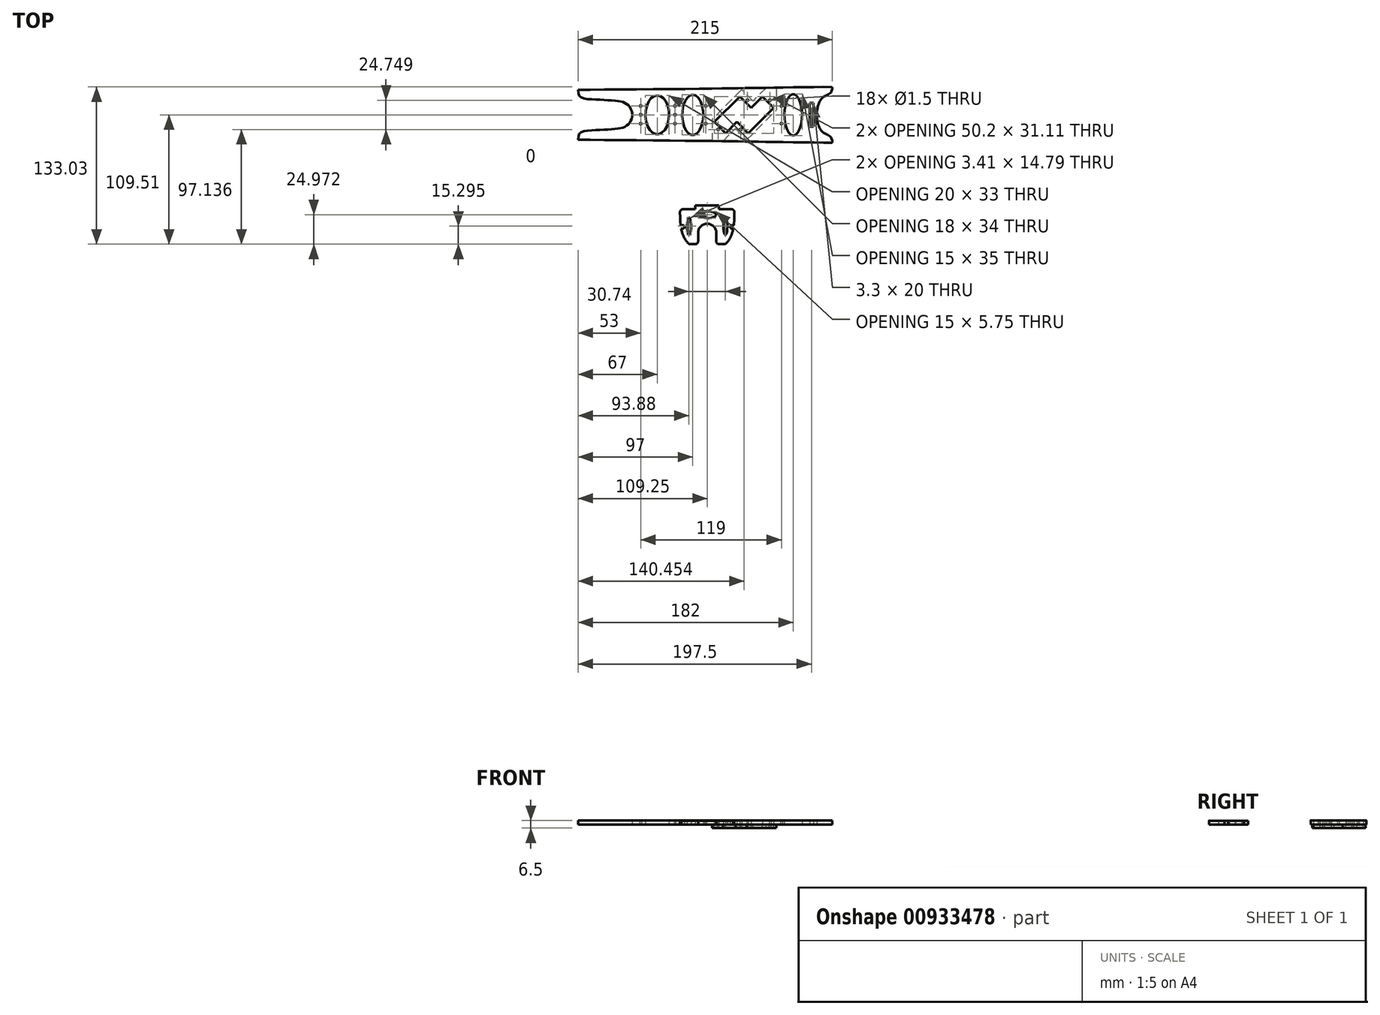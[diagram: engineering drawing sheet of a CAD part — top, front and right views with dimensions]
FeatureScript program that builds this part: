
annotation { "Feature Type Name" : "Feature", "Feature Type Description" : "" }
export const myFeature = defineFeature(function(context is Context, id is Id, definition is map)
    precondition{}
    {
        {
            var Q0;
            Q0=qCreatedBy(makeId("Top.planeOp"),FACE);
            var sketch = newSketch(context, id + "F0", { "sketchPlane" : qUnion([Q0])});
            skLineSegment(sketch, "E0", {"start": v(-109.25, -3.3) * mm, "end": v(-109.25, -45.3) * mm, "construction": true});
            skPoint(sketch, "E1", {"position": v(-109.25, -24.3) * mm});
            skLineSegment(sketch, "E2", {"start": v(105.75, -1.8) * mm, "end": v(105.75, -46.8) * mm, "construction": true});
            skPoint(sketch, "E3", {"position": v(105.75, -24.3) * mm});
            skLineSegment(sketch, "E4", {"start": v(-109.25, -24.3) * mm, "end": v(105.75, -24.3) * mm, "construction": true});
            skPoint(sketch, "E5", {"position": v(0, 0) * mm});
            skSolve(sketch);
        }
        {
            var Q0;
            Q0=qCreatedBy(makeId("Top.planeOp"),FACE);
            var sketch = newSketch(context, id + "F1", { "sketchPlane" : qUnion([Q0])});
            skLineSegment(sketch, "E6.0", {"start": v(-109.25, -3.3) * mm, "end": v(-109.25, -45.3) * mm, "construction": true});
            skLineSegment(sketch, "E7.0", {"start": v(-109.25, -24.3) * mm, "end": v(105.75, -24.3) * mm, "construction": true});
            skLineSegment(sketch, "E8.0", {"start": v(105.75, -0.8) * mm, "end": v(105.75, -46.8) * mm, "construction": true});
            skPoint(sketch, "E9.0", {"position": v(105.75, -24.3) * mm});
            skPoint(sketch, "E10.0", {"position": v(105.75, -1.8) * mm});
            skPoint(sketch, "E11.0", {"position": v(105.75, -46.8) * mm});
            skPoint(sketch, "E12.0", {"position": v(-109.25, -45.3) * mm});
            skPoint(sketch, "E13.0", {"position": v(-109.25, -24.3) * mm});
            skPoint(sketch, "E14.0", {"position": v(-109.25, -3.3) * mm});
            skFitSpline(sketch, "E15", {"points": [v(-109.25, -3.3) * mm, v(-1.69, -2.2) * mm, v(33.76, -1.65) * mm, v(60.11, -1.3) * mm, v(105.75, -0.8) * mm], "startDerivative": vector(214.94, 3.55) * mm, "endDerivative": vector(149.57, -1.3) * mm});
            skFitSpline(sketch, "E16", {"points": [v(-109.25, -3.3) * mm, v(-107.75, -8.59) * mm, v(-103.34, -10.65) * mm, v(-92.47, -11.5) * mm, v(-82.9, -12) * mm, v(-75.3, -12.62) * mm, v(-71.83, -13.28) * mm, v(-68.83, -14.68) * mm, v(-66.4, -16.56) * mm, v(-64.61, -19.28) * mm, v(-63.68, -22.18) * mm, v(-63.5, -24.3) * mm], "startDerivative": vector(0, -79.4) * mm, "endDerivative": vector(0, -33.77) * mm});
            skFitSpline(sketch, "E17", {"points": [v(105.75, -0.8) * mm, v(104.77, -5.14) * mm, v(102.97, -6.7) * mm, v(99.97, -8.21) * mm, v(97.34, -10) * mm, v(95.85, -11.78) * mm, v(94.53, -14.5) * mm, v(93.6, -17.21) * mm, v(93.03, -20.22) * mm, v(92.86, -22.42) * mm, v(92.86, -24.3) * mm], "startDerivative": vector(0, -44.94) * mm, "endDerivative": vector(0, -23.1) * mm});
            skLineSegment(sketch, "E18", {"start": v(37.21, -18.29) * mm, "end": v(27.67, -8.74) * mm});
            skLineSegment(sketch, "E19", {"start": v(27.67, -8.74) * mm, "end": v(6.1, -30.31) * mm});
            skLineSegment(sketch, "E20", {"start": v(6.1, -30.31) * mm, "end": v(15.65, -39.86) * mm});
            skLineSegment(sketch, "E21", {"start": v(15.65, -39.86) * mm, "end": v(37.21, -18.29) * mm});
            skPoint(sketch, "E22", {"position": v(32.44, -13.52) * mm});
            skPoint(sketch, "E23", {"position": v(10.87, -35.08) * mm});
            skLineSegment(sketch, "E24", {"start": v(32.44, -13.52) * mm, "end": v(10.87, -35.08) * mm, "construction": true});
            skCircle(sketch, "E25", {"center": v(26.43, -19.53) * mm, "radius": 17 * mm, "construction": true});
            skPoint(sketch, "E26", {"position": v(21.66, -24.3) * mm});
            skCircle(sketch, "E27", {"center": v(26.43, -19.53) * mm, "radius": 13 * mm, "construction": true});
            skLineSegment(sketch, "E28", {"start": v(6.1, -30.31) * mm, "end": v(2.92, -33.5) * mm, "construction": true});
            skLineSegment(sketch, "E29", {"start": v(2.92, -33.5) * mm, "end": v(12.47, -43.04) * mm, "construction": true});
            skLineSegment(sketch, "E30", {"start": v(12.47, -43.04) * mm, "end": v(15.65, -39.86) * mm, "construction": true});
            skLineSegment(sketch, "E31", {"start": v(27.67, -8.74) * mm, "end": v(30.85, -5.56) * mm, "construction": true});
            skLineSegment(sketch, "E32", {"start": v(30.85, -5.56) * mm, "end": v(40.4, -15.1) * mm, "construction": true});
            skLineSegment(sketch, "E33", {"start": v(40.4, -15.1) * mm, "end": v(37.21, -18.29) * mm, "construction": true});
            skLineSegment(sketch, "E34", {"start": v(25.2, -30.31) * mm, "end": v(34.74, -39.86) * mm});
            skLineSegment(sketch, "E35", {"start": v(34.74, -39.86) * mm, "end": v(56.3, -18.29) * mm});
            skLineSegment(sketch, "E36", {"start": v(56.3, -18.29) * mm, "end": v(46.76, -8.74) * mm});
            skLineSegment(sketch, "E37", {"start": v(46.76, -8.74) * mm, "end": v(25.2, -30.31) * mm});
            skPoint(sketch, "E38", {"position": v(29.97, -35.08) * mm});
            skPoint(sketch, "E39", {"position": v(51.53, -13.52) * mm});
            skLineSegment(sketch, "E40", {"start": v(29.97, -35.08) * mm, "end": v(51.53, -13.52) * mm, "construction": true});
            skCircle(sketch, "E41", {"center": v(35.98, -29.07) * mm, "radius": 17 * mm, "construction": true});
            skPoint(sketch, "E42", {"position": v(40.75, -24.3) * mm});
            skCircle(sketch, "E43", {"center": v(35.98, -29.07) * mm, "radius": 13 * mm, "construction": true});
            skLineSegment(sketch, "E44", {"start": v(56.3, -18.29) * mm, "end": v(59.49, -15.1) * mm, "construction": true});
            skLineSegment(sketch, "E45", {"start": v(59.49, -15.1) * mm, "end": v(49.94, -5.56) * mm, "construction": true});
            skLineSegment(sketch, "E46", {"start": v(49.94, -5.56) * mm, "end": v(46.76, -8.74) * mm, "construction": true});
            skLineSegment(sketch, "E47", {"start": v(34.74, -39.86) * mm, "end": v(31.56, -43.04) * mm, "construction": true});
            skLineSegment(sketch, "E48", {"start": v(31.56, -43.04) * mm, "end": v(22.01, -33.5) * mm, "construction": true});
            skLineSegment(sketch, "E49", {"start": v(22.01, -33.5) * mm, "end": v(25.2, -30.31) * mm, "construction": true});
            skFitSpline(sketch, "E50.MirrorCS", {"points": [v(-109.25, -45.3) * mm, v(-1.69, -46.4) * mm, v(33.76, -46.95) * mm, v(60.11, -47.3) * mm, v(105.75, -47.8) * mm], "startDerivative": vector(214.94, -3.55) * mm, "endDerivative": vector(149.57, 1.3) * mm});
            skFitSpline(sketch, "E51.MirrorCS", {"points": [v(-109.25, -45.3) * mm, v(-107.75, -40.01) * mm, v(-103.34, -37.95) * mm, v(-92.47, -37.1) * mm, v(-82.9, -36.6) * mm, v(-75.3, -35.98) * mm, v(-71.83, -35.32) * mm, v(-68.83, -33.92) * mm, v(-66.4, -32.04) * mm, v(-64.61, -29.32) * mm, v(-63.68, -26.42) * mm, v(-63.5, -24.3) * mm], "startDerivative": vector(0, 79.4) * mm, "endDerivative": vector(0, 33.77) * mm});
            skFitSpline(sketch, "E52.MirrorCS", {"points": [v(105.75, -47.8) * mm, v(104.77, -43.46) * mm, v(102.97, -41.9) * mm, v(99.97, -40.39) * mm, v(97.34, -38.6) * mm, v(95.85, -36.82) * mm, v(94.53, -34.1) * mm, v(93.6, -31.39) * mm, v(93.03, -28.38) * mm, v(92.86, -26.18) * mm, v(92.86, -24.3) * mm], "startDerivative": vector(0, 44.94) * mm, "endDerivative": vector(0, 23.1) * mm});
            skEllipse(sketch, "E53", {"center": v(72.75, -24.3) * mm, "majorRadius": 7.5 * mm, "minorRadius": 17.5 * mm, "majorAxis": v(-1, 0)});
            skEllipse(sketch, "E54", {"center": v(-12.25, -24.3) * mm, "majorRadius": 9 * mm, "minorRadius": 17 * mm, "majorAxis": v(1, 0)});
            skEllipse(sketch, "E55", {"center": v(-42.25, -24.3) * mm, "majorRadius": 10 * mm, "minorRadius": 16.5 * mm, "majorAxis": v(1, 0)});
            skLineSegment(sketch, "E56", {"start": v(53.12, -11.93) * mm, "end": v(28.38, -36.67) * mm, "construction": true});
            skLineSegment(sketch, "E57", {"start": v(9.28, -36.67) * mm, "end": v(34.03, -11.93) * mm, "construction": true});
            skCircle(sketch, "E58", {"center": v(53.12, -11.93) * mm, "radius": 0.75 * mm});
            skCircle(sketch, "E59", {"center": v(34.03, -11.93) * mm, "radius": 0.75 * mm});
            skCircle(sketch, "E60", {"center": v(9.28, -36.67) * mm, "radius": 0.75 * mm});
            skCircle(sketch, "E61", {"center": v(28.38, -36.67) * mm, "radius": 0.75 * mm});
            skLineSegment(sketch, "E62", {"start": v(62.75, -16.8) * mm, "end": v(62.75, -31.8) * mm, "construction": true});
            skPoint(sketch, "E63", {"position": v(62.75, -24.3) * mm});
            skCircle(sketch, "E64", {"center": v(62.75, -16.8) * mm, "radius": 0.75 * mm});
            skCircle(sketch, "E65", {"center": v(62.75, -31.8) * mm, "radius": 0.75 * mm});
            skLineSegment(sketch, "E66", {"start": v(-27.25, -16.8) * mm, "end": v(-27.25, -31.8) * mm, "construction": true});
            skPoint(sketch, "E67", {"position": v(-27.25, -24.3) * mm});
            skCircle(sketch, "E68", {"center": v(-27.25, -16.8) * mm, "radius": 0.75 * mm});
            skCircle(sketch, "E69", {"center": v(-27.25, -31.8) * mm, "radius": 0.75 * mm});
            skLineSegment(sketch, "E70", {"start": v(-56.25, -16.8) * mm, "end": v(-56.25, -31.8) * mm, "construction": true});
            skPoint(sketch, "E71", {"position": v(-56.25, -24.3) * mm});
            skCircle(sketch, "E72", {"center": v(-56.25, -16.8) * mm, "radius": 0.75 * mm});
            skCircle(sketch, "E73", {"center": v(-56.25, -31.8) * mm, "radius": 0.75 * mm});
            skPoint(sketch, "E74", {"position": v(-52.25, -24.3) * mm});
            skPoint(sketch, "E75", {"position": v(-21.25, -24.3) * mm});
            skPoint(sketch, "E76", {"position": v(-3.25, -24.3) * mm});
            skPoint(sketch, "E77", {"position": v(-1.75, -24.3) * mm});
            skLineSegment(sketch, "E78.bottom", {"start": v(89.9, -34.3) * mm, "end": v(86.6, -34.3) * mm});
            skLineSegment(sketch, "E78.top", {"start": v(89.9, -14.3) * mm, "end": v(86.6, -14.3) * mm});
            skLineSegment(sketch, "E78.left", {"start": v(89.9, -34.3) * mm, "end": v(89.9, -14.3) * mm});
            skLineSegment(sketch, "E78.right", {"start": v(86.6, -34.3) * mm, "end": v(86.6, -14.3) * mm});
            skPoint(sketch, "E78.middle", {"position": v(88.25, -24.3) * mm});
            skLineSegment(sketch, "E79", {"start": v(-1.25, -16.8) * mm, "end": v(-1.25, -31.8) * mm, "construction": true});
            skPoint(sketch, "E80", {"position": v(-1.25, -24.3) * mm});
            skCircle(sketch, "E81", {"center": v(-1.25, -16.8) * mm, "radius": 0.75 * mm});
            skCircle(sketch, "E82", {"center": v(-1.25, -31.8) * mm, "radius": 0.75 * mm});
            skCircle(sketch, "E83", {"center": v(-56.25, -24.3) * mm, "radius": 0.75 * mm});
            skCircle(sketch, "E84", {"center": v(-27.25, -24.3) * mm, "radius": 0.75 * mm});
            skSolve(sketch);
        }
        {
            var Q0;
            Q0 = qSketchRegion(id + "F1", true);
            extrude(context, id + "F2", {"entities" : qUnion([Q0]), "depth" : 3.5 * mm, "offsetDistance" : 25 * mm});
        }
        {
            var Q0;
            Q0=qCreatedBy(makeId("Top.planeOp"),FACE);
            var sketch = newSketch(context, id + "F3", { "sketchPlane" : qUnion([Q0])});
            skFitSpline(sketch, "E85.0", {"points": [v(-109.25, -45.3) * mm, v(-82.91, -45.74) * mm, v(-1.27, -46.23) * mm, v(32.74, -47) * mm, v(59.45, -47.22) * mm, v(93.81, -47.9) * mm, v(105.75, -47.8) * mm]});
            skLineSegment(sketch, "E86.0", {"start": v(15.65, -39.86) * mm, "end": v(25.2, -30.31) * mm});
            skLineSegment(sketch, "E87.0", {"start": v(25.2, -30.31) * mm, "end": v(34.74, -39.86) * mm});
            skLineSegment(sketch, "E88.0", {"start": v(34.74, -39.86) * mm, "end": v(56.3, -18.29) * mm});
            skLineSegment(sketch, "E89.0", {"start": v(56.3, -18.29) * mm, "end": v(46.76, -8.74) * mm});
            skLineSegment(sketch, "E90.0", {"start": v(46.76, -8.74) * mm, "end": v(37.21, -18.29) * mm});
            skLineSegment(sketch, "E91.0", {"start": v(37.21, -18.29) * mm, "end": v(27.67, -8.74) * mm});
            skLineSegment(sketch, "E92.0", {"start": v(27.67, -8.74) * mm, "end": v(6.1, -30.31) * mm});
            skLineSegment(sketch, "E93.0", {"start": v(6.1, -30.31) * mm, "end": v(15.65, -39.86) * mm});
            skCircle(sketch, "E94.0", {"center": v(34.03, -11.93) * mm, "radius": 0.75 * mm});
            skCircle(sketch, "E95.0", {"center": v(53.12, -11.93) * mm, "radius": 0.75 * mm});
            skCircle(sketch, "E96.0", {"center": v(28.38, -36.67) * mm, "radius": 0.75 * mm});
            skCircle(sketch, "E97.0", {"center": v(9.28, -36.67) * mm, "radius": 0.75 * mm});
            skLineSegment(sketch, "E98", {"start": v(4.1, -28.07) * mm, "end": v(4.1, -46.47) * mm});
            skLineSegment(sketch, "E99", {"start": v(58.3, -1.33) * mm, "end": v(58.3, -20.53) * mm});
            skPoint(sketch, "E100.orphan", {"position": v(105.75, -0.8) * mm});
            skPoint(sketch, "E101.orphan", {"position": v(105.75, -47.8) * mm});
            skPoint(sketch, "E102.orphan", {"position": v(-109.25, -45.3) * mm});
            skPoint(sketch, "E103.orphan", {"position": v(-109.25, -3.3) * mm});
            skPoint(sketch, "E104", {"position": v(16.89, -19.53) * mm});
            skPoint(sketch, "E105", {"position": v(45.52, -29.07) * mm});
            skLineSegment(sketch, "E106.0", {"start": v(29.08, -3.09) * mm, "end": v(4.1, -28.07) * mm});
            skLineSegment(sketch, "E107.0", {"start": v(33.33, -45.51) * mm, "end": v(58.3, -20.53) * mm});
            skLineSegment(sketch, "E108.0", {"start": v(38.63, -12.63) * mm, "end": v(29.08, -3.09) * mm});
            skLineSegment(sketch, "E109.0", {"start": v(23.78, -35.97) * mm, "end": v(33.33, -45.51) * mm});
            skLineSegment(sketch, "E110.0", {"start": v(13.14, -46.6) * mm, "end": v(23.78, -35.97) * mm});
            skLineSegment(sketch, "E111.0", {"start": v(49.82, -1.44) * mm, "end": v(38.63, -12.63) * mm});
            skFitSpline(sketch, "E112.0", {"points": [v(-109.25, -3.3) * mm, v(-82.91, -2.86) * mm, v(-1.27, -2.37) * mm, v(32.74, -1.6) * mm, v(59.45, -1.38) * mm, v(93.81, -0.7) * mm, v(105.75, -0.8) * mm]});
            skSolve(sketch);
        }
        {
            var Q0;
            Q0 = qSketchRegion(id + "F3", true);
            extrude(context, id + "F4", {"entities" : qUnion([Q0]), "oppositeDirection" : true, "depth" : 3 * mm, "offsetDistance" : 25 * mm});
        }
        {
            var Q0;
            Q0=qCreatedBy(makeId("Top.planeOp"),FACE);
            var sketch = newSketch(context, id + "F5", { "sketchPlane" : qUnion([Q0])});
            skLineSegment(sketch, "E113.bottom", {"start": v(14.28, -133.8) * mm, "end": v(10.21, -133.8) * mm});
            skLineSegment(sketch, "E113.top", {"start": v(20.5, -104.16) * mm, "end": v(10, -104.16) * mm});
            skPoint(sketch, "E113.middle", {"position": v(0, -118.99) * mm});
            skLineSegment(sketch, "E114.top", {"start": v(10, -100.84) * mm, "end": v(-10, -100.84) * mm});
            skLineSegment(sketch, "E114.left", {"start": v(10, -104.16) * mm, "end": v(10, -100.84) * mm});
            skLineSegment(sketch, "E114.right", {"start": v(-10, -104.16) * mm, "end": v(-10, -100.84) * mm});
            skPoint(sketch, "E114.middle", {"position": v(0, -102.5) * mm});
            skPoint(sketch, "E114.middle.positionSnap0", {"position": v(0, -104.16) * mm});
            skPoint(sketch, "E114.centerSnap0", {"position": v(0, -104.16) * mm});
            skLineSegment(sketch, "E115.trimOffspring", {"start": v(-10, -104.16) * mm, "end": v(-20.5, -104.16) * mm});
            skArc(sketch, "E116", {"start": v(7.71, -124.16) * mm, "mid": v(0, -116.45) * mm, "end": v(-7.71, -124.16) * mm});
            skLineSegment(sketch, "E117", {"start": v(-7.71, -131.3) * mm, "end": v(-7.71, -124.16) * mm});
            skLineSegment(sketch, "E118", {"start": v(7.71, -131.3) * mm, "end": v(7.71, -124.16) * mm});
            skLineSegment(sketch, "E119.trimOffspring", {"start": v(-10.21, -133.8) * mm, "end": v(-14.28, -133.8) * mm});
            skPoint(sketch, "E120", {"position": v(0, -100.84) * mm});
            skFitSpline(sketch, "E121", {"points": [v(23, -104.16) * mm, v(15.36, -133.8) * mm], "startDerivative": vector(0, -36) * mm, "endDerivative": vector(-22.93, -23.1) * mm});
            skLineSegment(sketch, "E122", {"start": v(0, -100.84) * mm, "end": v(0, -146.1) * mm, "construction": true});
            skFitSpline(sketch, "E123.MirrorCS", {"points": [v(-23, -104.16) * mm, v(-15.36, -133.8) * mm], "startDerivative": vector(0, -36) * mm, "endDerivative": vector(22.93, -23.1) * mm});
            skPoint(sketch, "E113.right.start.orphan", {"position": v(-23, -133.8) * mm});
            skPoint(sketch, "E113.left.start.orphan", {"position": v(23, -133.8) * mm});
            skPoint(sketch, "E124.visualSharp", {"position": v(-7.71, -133.8) * mm});
            skArc(sketch, "E124.filletArc", {"start": v(-10.21, -133.8) * mm, "mid": v(-8.44, -133.08) * mm, "end": v(-7.71, -131.3) * mm});
            skPoint(sketch, "E125.visualSharp", {"position": v(7.71, -133.8) * mm});
            skArc(sketch, "E125.filletArc", {"start": v(7.71, -131.3) * mm, "mid": v(8.44, -133.08) * mm, "end": v(10.21, -133.8) * mm});
            skArc(sketch, "E126.filletArc", {"start": v(-16.13, -132.99) * mm, "mid": v(-15.3, -133.6) * mm, "end": v(-14.28, -133.8) * mm});
            skArc(sketch, "E127.filletArc", {"start": v(14.28, -133.8) * mm, "mid": v(15.3, -133.6) * mm, "end": v(16.13, -132.99) * mm});
            skEllipse(sketch, "E128", {"center": v(0, -108.84) * mm, "majorRadius": 7.5 * mm, "minorRadius": 2.87 * mm, "majorAxis": v(1, 0)});
            skLineSegment(sketch, "E129", {"start": v(-23, -104.16) * mm, "end": v(-7.74, -132.86) * mm, "construction": true});
            skEllipse(sketch, "E130", {"center": v(-15.37, -118.51) * mm, "majorRadius": 7.4 * mm, "minorRadius": 1.7 * mm, "majorAxis": v(0, 1)});
            skEllipse(sketch, "E131.MirrorC", {"center": v(15.37, -118.51) * mm, "majorRadius": 7.4 * mm, "minorRadius": 1.7 * mm, "majorAxis": v(0, 1)});
            skLineSegment(sketch, "E132", {"start": v(-32, -119.16) * mm, "end": v(52.44, -119.16) * mm, "construction": true});
            skArc(sketch, "E133", {"start": v(-20.77, -120.66) * mm, "mid": v(-19.27, -119.16) * mm, "end": v(-20.77, -117.66) * mm});
            skLineSegment(sketch, "E134", {"start": v(-20.77, -117.66) * mm, "end": v(-22.5, -117.66) * mm});
            skLineSegment(sketch, "E135", {"start": v(-20.77, -120.66) * mm, "end": v(-22.03, -120.66) * mm});
            skFitSpline(sketch, "E136.trimOffspring", {"points": [v(-23, -104.16) * mm, v(-15.36, -133.8) * mm], "startDerivative": vector(0, -36) * mm, "endDerivative": vector(22.93, -23.1) * mm});
            skLineSegment(sketch, "E137", {"start": v(20.99, -117.66) * mm, "end": v(22.5, -117.66) * mm});
            skLineSegment(sketch, "E138", {"start": v(20.99, -120.66) * mm, "end": v(22.03, -120.66) * mm});
            skArc(sketch, "E139", {"start": v(20.99, -117.66) * mm, "mid": v(19.49, -119.16) * mm, "end": v(20.99, -120.66) * mm});
            skArc(sketch, "E140.filletArc", {"start": v(-20.5, -104.16) * mm, "mid": v(-22.27, -104.9) * mm, "end": v(-23, -106.67) * mm});
            skArc(sketch, "E141.filletArc", {"start": v(23, -106.67) * mm, "mid": v(22.27, -104.9) * mm, "end": v(20.5, -104.16) * mm});
            skSolve(sketch);
        }
        {
            var Q0;
            Q0=makeQuery(id+"F5.imprint","IMPRINT",FACE,{"disambiguationData":[TD([[makeQuery(id+"F5.imprint","IMPRINT",EDGE,{"derivedFrom":sQuery(id+"F5.wireOp",EDGE,"E113.bottom")}),-1.0]])]});
            extrude(context, id + "F6", {"entities" : qUnion([Q0]), "depth" : 3.2 * mm, "offsetDistance" : 25 * mm});
        }
    });
